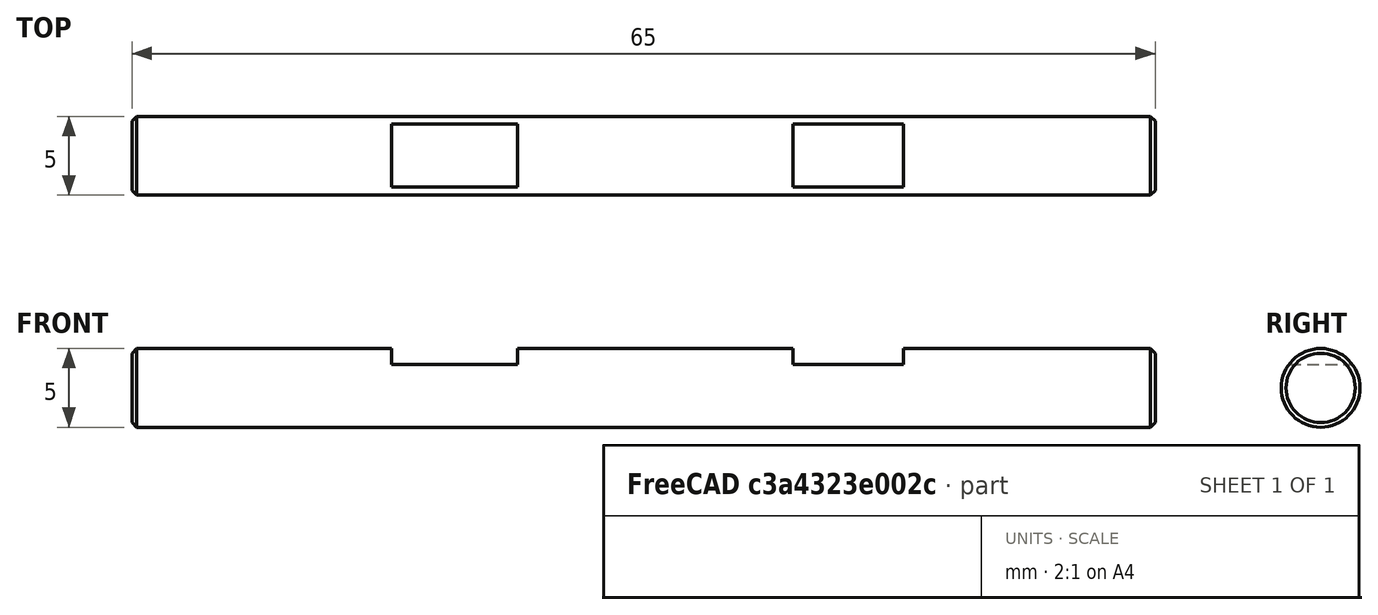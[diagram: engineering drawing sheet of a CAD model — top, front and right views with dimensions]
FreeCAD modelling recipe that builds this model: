
FCSTD DOCUMENT  (FreeCAD 0.19R24291 (Git))
Label: 5x65-shaft
License: Other
LicenseURL: GPL3
objects: TechDraw::DrawViewDimension×6, TechDraw::DrawViewPart×4, Sketcher::SketchObject×2, PartDesign::Pad×1, PartDesign::Pocket×1, PartDesign::Chamfer×1, PartDesign::Body×1, TechDraw::DrawSVGTemplate×1, TechDraw::DrawPage×1
note: 9 computed .brp shape members not serialized (recipe doc carries the construction recipe); baked Part::Feature solids carry a one-line shape summary decoded from their .brp

FEATURE [Sketcher::SketchObject] Sketch
  FullyConstrained = true
  MapMode = 5
  Placement = pos=(0,0,0) rot=(0.57735,0.57735,0.57735;2.0944rad)
  Support = -> [YZ_Plane]
  sketch-geometry (1):
    g0: Circle CenterX=0 CenterY=0 CenterZ=0 NormalX=0 NormalY=0 NormalZ=1 AngleXU=0 Radius=2.5
  constraints (2):
    c: Coincident(g0,g-1)
    c: Radius(g0) = 2.5
FEATURE [PartDesign::Pad] Pad
  Direction = (1,1,1)
  Length = 65
  Length2 = 100
  Placement = pos=(0,0,0) rot=(0.57735,0.57735,0.57735;2.0944rad)
  Profile = -> Sketch
  Type = 0
FEATURE [Sketcher::SketchObject] Sketch001
  AttachmentOffset = pos=(0,0,3) rot=(0,0,1;0rad)
  FullyConstrained = true
  MapMode = 5
  Placement = pos=(0,0,3) rot=(0,0,1;0rad)
  Support = -> [XY_Plane]
  sketch-geometry (8):
    g0: LineSegment StartX=16.5 StartY=3 StartZ=0 EndX=24.5 EndY=3 EndZ=0
    g1: LineSegment StartX=24.5 StartY=3 StartZ=0 EndX=24.5 EndY=-3 EndZ=0
    g2: LineSegment StartX=24.5 StartY=-3 StartZ=0 EndX=16.5 EndY=-3 EndZ=0
    g3: LineSegment StartX=16.5 StartY=-3 StartZ=0 EndX=16.5 EndY=3 EndZ=0
    g4: LineSegment StartX=42 StartY=3 StartZ=0 EndX=49 EndY=3 EndZ=0
    g5: LineSegment StartX=49 StartY=3 StartZ=0 EndX=49 EndY=-3 EndZ=0
    g6: LineSegment StartX=49 StartY=-3 StartZ=0 EndX=42 EndY=-3 EndZ=0
    g7: LineSegment StartX=42 StartY=-3 StartZ=0 EndX=42 EndY=3 EndZ=0
  constraints (24):
    c: Coincident(g0,g1)
    c: Coincident(g1,g2)
    c: Coincident(g2,g3)
    c: Coincident(g3,g0)
    c: Horizontal(g0)
    c: Horizontal(g2)
    c: Vertical(g1)
    c: Vertical(g3)
    c: Coincident(g4,g5)
    c: Coincident(g5,g6)
    c: Coincident(g6,g7)
    c: Coincident(g7,g4)
    c: Horizontal(g4)
    c: Horizontal(g6)
    c: Vertical(g5)
    c: Vertical(g7)
    c: DistanceX(g4,g4) = 7
    c: DistanceX(g0,g0) = 8
    c: DistanceY(g1,g1) = 6
    c: DistanceY(g5,g5) = 6
    c: DistanceY(g-1,g0) = 3
    c: DistanceY(g-1,g4) = 3
    c: DistanceX(g-1,g0) = 16.5
    c: DistanceX(g-1,g4) = 42
FEATURE [PartDesign::Pocket] Pocket
  BaseFeature = -> Pad
  Length = 1.5
  Length2 = 100
  Placement = pos=(0,0,0) rot=(0.57735,0.57735,0.57735;2.0944rad)
  Profile = -> Sketch001
  Type = 0
FEATURE [PartDesign::Chamfer] Chamfer
  Angle = 45
  Base = -> Pocket [Edge1,Edge3]
  BaseFeature = -> Pocket
  ChamferType = 0
  FlipDirection = false
  Placement = pos=(0,0,0) rot=(0.57735,0.57735,0.57735;2.0944rad)
  Size = 0.3
  Size2 = 1
  SupportTransform = false
FEATURE [PartDesign::Body] Body  label="5x65-shaft"
  Group = -> [Sketch,Pad,Sketch001,Pocket,Chamfer]
  Origin = -> Origin
  Tip = -> Chamfer
FEATURE [TechDraw::DrawSVGTemplate] Template
  EditableTexts = Designed_by_Name=Chip; Drawing_number=001; FC-Date=2121-11-09; FC-SC=2:1; FC-SH=1/1; FC-Title=5x65mm shaft; Subtitle=z pulley connector; Weight=-
  Height = 210
  Orientation = 1
  Width = 297
FEATURE [TechDraw::DrawViewPart] View
  CoarseView = false
  Direction = (0,-1,0)
  Focus = 100
  HardHidden = false
  IsoCount = 0
  IsoHidden = false
  IsoVisible = false
  LockPosition = false
  Perspective = false
  Rotation = 0
  ScaleType = 0
  SeamHidden = false
  SeamVisible = true
  SmoothHidden = false
  SmoothVisible = true
  Source = -> [Chamfer]
  X = 243.657
  XDirection = (0.816,0,0.408)
  Y = 154.538
FEATURE [TechDraw::DrawViewPart] View001
  CoarseView = false
  Direction = (0,-1,0)
  Focus = 100
  HardHidden = false
  IsoCount = 0
  IsoHidden = false
  IsoVisible = false
  LockPosition = false
  Perspective = false
  Rotation = 0
  Scale = 2
  ScaleType = 0
  SeamHidden = false
  SeamVisible = true
  SmoothHidden = false
  SmoothVisible = true
  Source = -> [Chamfer]
  X = 102.405
  XDirection = (1,0,0)
  Y = 86.0178
FEATURE [TechDraw::DrawViewPart] View002
  CoarseView = false
  Direction = (-1,0,0)
  Focus = 100
  HardHidden = false
  IsoCount = 0
  IsoHidden = false
  IsoVisible = false
  LockPosition = false
  Perspective = false
  Rotation = 0
  Scale = 2
  ScaleType = 0
  SeamHidden = false
  SeamVisible = true
  SmoothHidden = false
  SmoothVisible = true
  Source = -> [Body]
  X = 206.829
  XDirection = (0,-1,0)
  Y = 87.6645
FEATURE [TechDraw::DrawViewPart] View003
  CoarseView = false
  Direction = (0,0,1)
  Focus = 100
  HardHidden = false
  IsoCount = 0
  IsoHidden = false
  IsoVisible = false
  LockPosition = false
  Perspective = false
  Rotation = 0
  Scale = 2
  ScaleType = 0
  SeamHidden = false
  SeamVisible = true
  SmoothHidden = false
  SmoothVisible = true
  Source = -> [Body]
  X = 100.977
  XDirection = (1,0,0)
  Y = 172.315
FEATURE [TechDraw::DrawViewDimension] Dimension
  Arbitrary = false
  ArbitraryTolerances = false
  EqualTolerance = true
  FormatSpec = %.2f
  FormatSpecOverTolerance = %+.2f
  FormatSpecUnderTolerance = %+.2f
  Inverted = false
  LockPosition = false
  MeasureType = 1
  OverTolerance = 0
  References2D = -> [View001]
  Rotation = 0
  ScaleType = 0
  TheoreticalExact = false
  Type = 1
  UnderTolerance = 0
  X = 0
  Y = -15.9867
FEATURE [TechDraw::DrawViewDimension] Dimension001
  Arbitrary = false
  ArbitraryTolerances = false
  EqualTolerance = true
  FormatSpec = %.2f
  FormatSpecOverTolerance = %+.2f
  FormatSpecUnderTolerance = %+.2f
  Inverted = false
  LockPosition = false
  MeasureType = 1
  OverTolerance = 0
  References2D = -> [View001]
  Rotation = 0
  ScaleType = 0
  TheoreticalExact = false
  Type = 1
  UnderTolerance = 0
  X = -52.6552
  Y = 22.9191
FEATURE [TechDraw::DrawViewDimension] Dimension002
  Arbitrary = false
  ArbitraryTolerances = false
  EqualTolerance = true
  FormatSpec = %.2f
  FormatSpecOverTolerance = %+.2f
  FormatSpecUnderTolerance = %+.2f
  Inverted = false
  LockPosition = false
  MeasureType = 1
  OverTolerance = 0
  References2D = -> [View001]
  Rotation = 0
  ScaleType = 0
  TheoreticalExact = false
  Type = 1
  UnderTolerance = 0
  X = -23.2009
  Y = 22.8195
FEATURE [TechDraw::DrawViewDimension] Dimension003
  Arbitrary = false
  ArbitraryTolerances = false
  EqualTolerance = true
  FormatSpec = %.2f
  FormatSpecOverTolerance = %+.2f
  FormatSpecUnderTolerance = %+.2f
  Inverted = false
  LockPosition = false
  MeasureType = 1
  OverTolerance = 0
  References2D = -> [View001]
  Rotation = 0
  ScaleType = 0
  TheoreticalExact = false
  Type = 1
  UnderTolerance = 0
  X = 4.37669
  Y = 22.8994
FEATURE [TechDraw::DrawViewDimension] Dimension004
  Arbitrary = false
  ArbitraryTolerances = false
  EqualTolerance = true
  FormatSpec = %.2f
  FormatSpecOverTolerance = %+.2f
  FormatSpecUnderTolerance = %+.2f
  Inverted = false
  LockPosition = false
  MeasureType = 1
  OverTolerance = 0
  References2D = -> [View001]
  Rotation = 0
  ScaleType = 0
  TheoreticalExact = false
  Type = 1
  UnderTolerance = 0
  X = 25.5175
  Y = 22.8281
FEATURE [TechDraw::DrawViewDimension] Dimension005
  Arbitrary = false
  ArbitraryTolerances = false
  EqualTolerance = true
  FormatSpec = ⌀%.2f
  FormatSpecOverTolerance = %+.2f
  FormatSpecUnderTolerance = %+.2f
  Inverted = false
  LockPosition = false
  MeasureType = 1
  OverTolerance = 0
  References2D = -> [View002]
  Rotation = 0
  ScaleType = 0
  TheoreticalExact = false
  Type = 5
  UnderTolerance = 0
  X = 11.44
  Y = 12.5798
FEATURE [TechDraw::DrawPage] Page
  KeepUpdated = true
  NextBalloonIndex = 1
  ProjectionType = 0
  Template = -> Template
  Views = -> [View,View001,View002,View003,Dimension,Dimension001,Dimension002,Dimension003,Dimension004,Dimension005]
